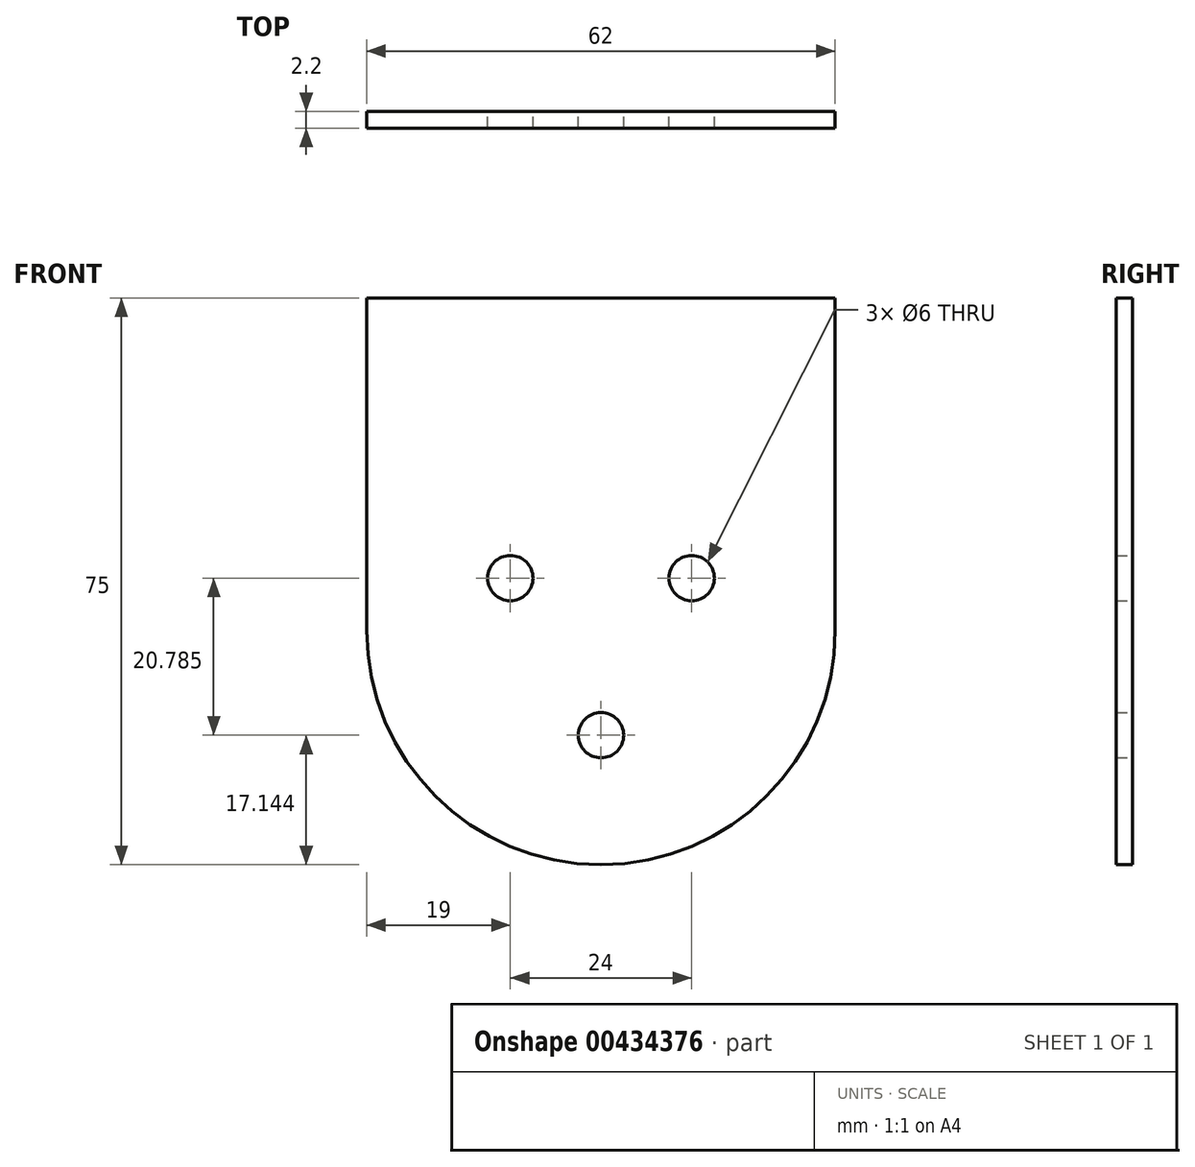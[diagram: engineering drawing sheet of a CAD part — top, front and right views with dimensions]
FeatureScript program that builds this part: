
annotation { "Feature Type Name" : "Feature", "Feature Type Description" : "" }
export const myFeature = defineFeature(function(context is Context, id is Id, definition is map)
    precondition{}
    {
        {
            var Q0;
            Q0=qCreatedBy(makeId("Front.planeOp"),FACE);
            var sketch = newSketch(context, id + "F0", { "sketchPlane" : qUnion([Q0])});
            skArc(sketch, "E0", {"start": v(0, -31) * mm, "mid": v(21.92, -21.92) * mm, "end": v(31, 0) * mm});
            skLineSegment(sketch, "E1", {"start": v(31, 0) * mm, "end": v(31, 44) * mm});
            skLineSegment(sketch, "E2", {"start": v(0, -44.96) * mm, "end": v(0, 184.97) * mm, "construction": true});
            skArc(sketch, "E3.1.0", {"start": v(9.4, 5.43) * mm, "mid": v(10.5, 9.53) * mm, "end": v(14.6, 8.43) * mm});
            skArc(sketch, "E3.1.1", {"start": v(9.4, 5.43) * mm, "mid": v(13.5, 4.33) * mm, "end": v(14.6, 8.43) * mm});
            skPoint(sketch, "E3.center", {"position": v(0, 28) * mm});
            skLineSegment(sketch, "E4", {"start": v(0, 0) * mm, "end": v(12, 6.93) * mm, "construction": true});
            skArc(sketch, "E5", {"start": v(0, -31) * mm, "mid": v(31, 0) * mm, "end": v(0, 31) * mm, "construction": true});
            skPoint(sketch, "E6.MirrorCS.end.orphan", {"position": v(0, -16.86) * mm});
            skPoint(sketch, "E7.MirrorP", {"position": v(0, -10.86) * mm});
            skArc(sketch, "E8.MirrorCS", {"start": v(-9.4, 5.43) * mm, "mid": v(-10.5, 9.53) * mm, "end": v(-14.6, 8.43) * mm});
            skArc(sketch, "E9.MirrorCS", {"start": v(-9.4, 5.43) * mm, "mid": v(-13.5, 4.33) * mm, "end": v(-14.6, 8.43) * mm});
            skLineSegment(sketch, "E10.MirrorCS", {"start": v(0, 0) * mm, "end": v(-12, 6.93) * mm, "construction": true});
            skArc(sketch, "E11.MirrorCS", {"start": v(0, -31) * mm, "mid": v(-21.92, -21.92) * mm, "end": v(-31, 0) * mm});
            skArc(sketch, "E12.MirrorCS", {"start": v(0, -31) * mm, "mid": v(-31, 0) * mm, "end": v(0, 31) * mm, "construction": true});
            skLineSegment(sketch, "E13.MirrorCS", {"start": v(-31, 0) * mm, "end": v(-31, 44) * mm});
            skCircle(sketch, "E14", {"center": v(0, 0) * mm, "radius": 13.86 * mm, "construction": true});
            skCircle(sketch, "E15", {"center": v(0, -13.86) * mm, "radius": 3 * mm});
            skLineSegment(sketch, "E16", {"start": v(-43.13, 44) * mm, "end": v(51.96, 44) * mm, "construction": true});
            skLineSegment(sketch, "E17", {"start": v(-31, 44) * mm, "end": v(31, 44) * mm});
            skSolve(sketch);
        }
        {
            var Q0;
            Q0=qSketchRegion(id+"F0",true);
            extrude(context, id + "F1", {"entities" : qUnion([Q0]), "depth" : 2.2 * mm});
        }
    });
